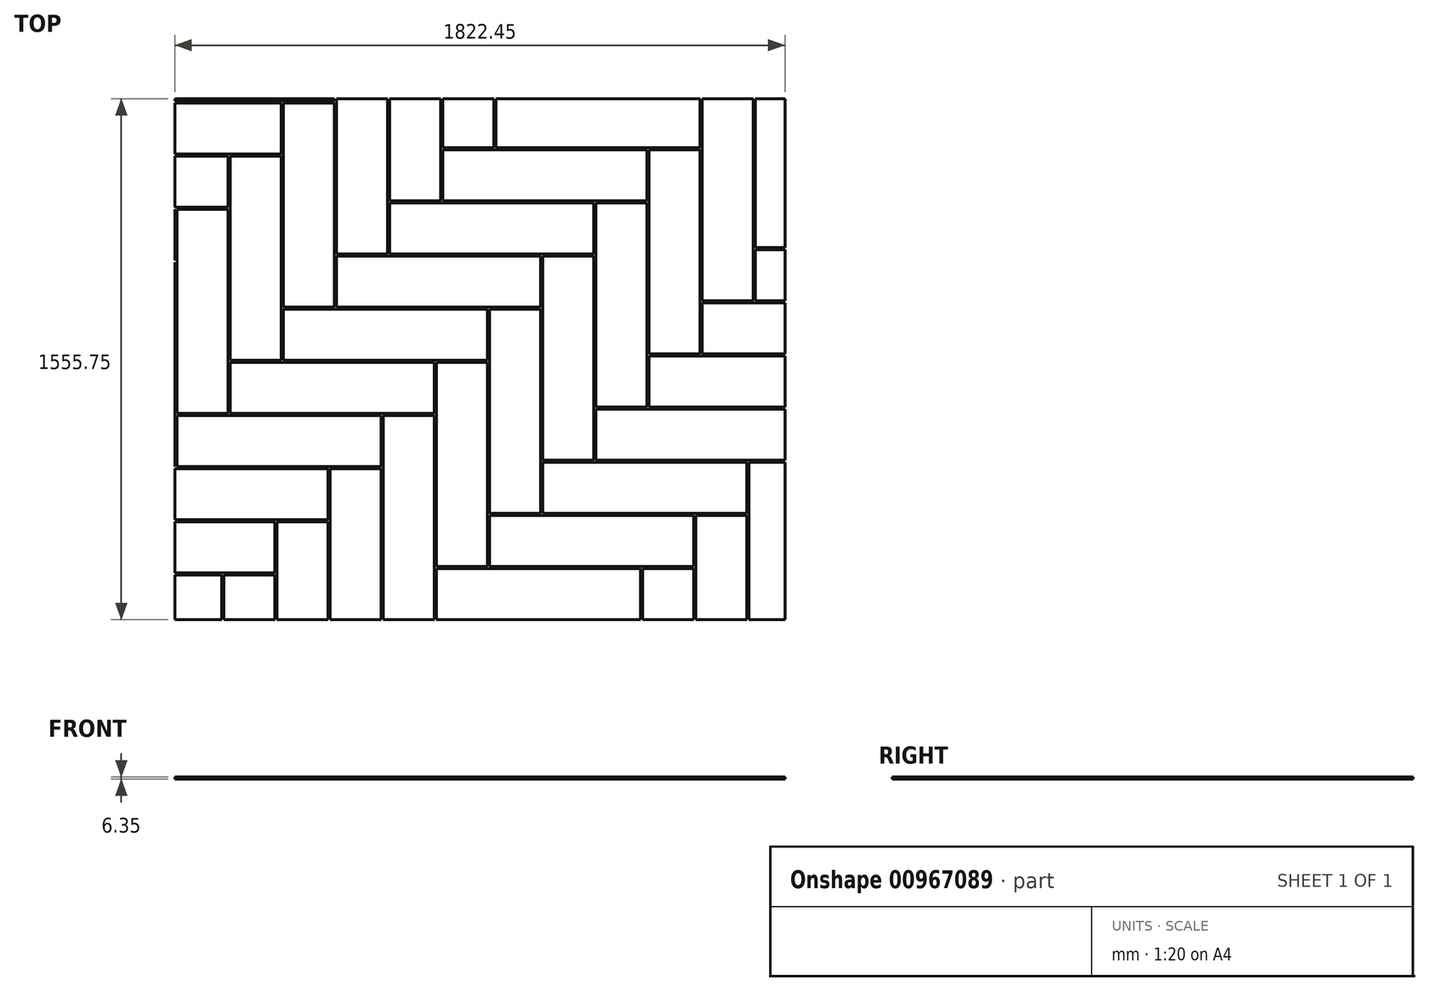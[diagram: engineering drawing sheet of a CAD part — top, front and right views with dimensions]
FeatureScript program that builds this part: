
annotation { "Feature Type Name" : "Feature", "Feature Type Description" : "" }
export const myFeature = defineFeature(function(context is Context, id is Id, definition is map)
    precondition{}
    {
        {
            var Q0;
            Q0=qCreatedBy(makeId("Top.planeOp"),FACE);
            var sketch = newSketch(context, id + "F0", { "sketchPlane" : qUnion([Q0])});
            skLineSegment(sketch, "E0", {"start": v(0, 2298.7) * mm, "end": v(0, 0) * mm});
            skLineSegment(sketch, "E1", {"start": v(0, 0) * mm, "end": v(1822.45, 0) * mm});
            skLineSegment(sketch, "E2", {"start": v(1822.45, 0) * mm, "end": v(1822.45, 1555.75) * mm});
            skLineSegment(sketch, "E3", {"start": v(1822.45, 1555.75) * mm, "end": v(1454.15, 1555.75) * mm});
            skLineSegment(sketch, "E4", {"start": v(1454.15, 1555.75) * mm, "end": v(1454.15, 2298.7) * mm});
            skLineSegment(sketch, "E5", {"start": v(1454.15, 2298.7) * mm, "end": v(0, 2298.7) * mm});
            skSolve(sketch);
        }
        {
            var Q0;
            Q0=qCreatedBy(makeId("Top.planeOp"),FACE);
            var sketch = newSketch(context, id + "F1", { "sketchPlane" : qUnion([Q0])});
            skLineSegment(sketch, "E6", {"start": v(863.6, 0) * mm, "end": v(863.6, -353.23) * mm, "construction": true});
            skLineSegment(sketch, "E7", {"start": v(1631.95, 0) * mm, "end": v(1631.95, -340.06) * mm, "construction": true});
            skLineSegment(sketch, "E8.bottom", {"start": v(781.93, 0) * mm, "end": v(1391.53, 0) * mm});
            skLineSegment(sketch, "E8.top", {"start": v(781.93, 152.4) * mm, "end": v(1391.53, 152.4) * mm});
            skLineSegment(sketch, "E8.left", {"start": v(781.93, 0) * mm, "end": v(781.93, 152.4) * mm});
            skLineSegment(sketch, "E8.right", {"start": v(1391.53, 0) * mm, "end": v(1391.53, 152.4) * mm});
            skLineSegment(sketch, "E9.bottom", {"start": v(781.93, 158.75) * mm, "end": v(934.33, 158.75) * mm});
            skLineSegment(sketch, "E9.top", {"start": v(781.93, 768.35) * mm, "end": v(934.33, 768.35) * mm});
            skLineSegment(sketch, "E9.left", {"start": v(781.93, 158.75) * mm, "end": v(781.93, 768.35) * mm});
            skLineSegment(sketch, "E9.right", {"start": v(934.33, 158.75) * mm, "end": v(934.33, 768.35) * mm});
            skLineSegment(sketch, "E10.bottom", {"start": v(940.68, 158.75) * mm, "end": v(1550.28, 158.75) * mm});
            skLineSegment(sketch, "E10.top", {"start": v(940.68, 311.15) * mm, "end": v(1550.28, 311.15) * mm});
            skLineSegment(sketch, "E10.left", {"start": v(940.68, 158.75) * mm, "end": v(940.68, 311.15) * mm});
            skLineSegment(sketch, "E10.right", {"start": v(1550.28, 158.75) * mm, "end": v(1550.28, 311.15) * mm});
            skLineSegment(sketch, "E11.bottom", {"start": v(940.68, 317.5) * mm, "end": v(1093.08, 317.5) * mm});
            skLineSegment(sketch, "E11.top", {"start": v(940.68, 927.1) * mm, "end": v(1093.08, 927.1) * mm});
            skLineSegment(sketch, "E11.left", {"start": v(940.68, 317.5) * mm, "end": v(940.68, 927.1) * mm});
            skLineSegment(sketch, "E11.right", {"start": v(1093.08, 317.5) * mm, "end": v(1093.08, 927.1) * mm});
            skLineSegment(sketch, "E12.bottom", {"start": v(775.58, 0) * mm, "end": v(623.18, 0) * mm});
            skLineSegment(sketch, "E12.top", {"start": v(775.58, 609.6) * mm, "end": v(623.18, 609.6) * mm});
            skLineSegment(sketch, "E12.left", {"start": v(775.58, 0) * mm, "end": v(775.58, 609.6) * mm});
            skLineSegment(sketch, "E12.right", {"start": v(623.18, 0) * mm, "end": v(623.18, 609.6) * mm});
            skLineSegment(sketch, "E13.bottom", {"start": v(616.83, 609.6) * mm, "end": v(7.23, 609.6) * mm});
            skLineSegment(sketch, "E13.top", {"start": v(616.83, 457.2) * mm, "end": v(7.23, 457.2) * mm});
            skLineSegment(sketch, "E13.left", {"start": v(616.83, 609.6) * mm, "end": v(616.83, 457.2) * mm});
            skLineSegment(sketch, "E13.right", {"start": v(7.23, 609.6) * mm, "end": v(7.23, 457.2) * mm});
            skLineSegment(sketch, "E14.bottom", {"start": v(616.83, 450.85) * mm, "end": v(464.43, 450.85) * mm});
            skLineSegment(sketch, "E14.top", {"start": v(616.83, -158.75) * mm, "end": v(464.43, -158.75) * mm});
            skLineSegment(sketch, "E14.left", {"start": v(616.83, 450.85) * mm, "end": v(616.83, -158.75) * mm});
            skLineSegment(sketch, "E14.right", {"start": v(464.43, 450.85) * mm, "end": v(464.43, -158.75) * mm});
            skLineSegment(sketch, "E15.bottom", {"start": v(458.08, 450.85) * mm, "end": v(-151.52, 450.85) * mm});
            skLineSegment(sketch, "E15.top", {"start": v(458.08, 298.45) * mm, "end": v(-151.52, 298.45) * mm});
            skLineSegment(sketch, "E15.left", {"start": v(458.08, 450.85) * mm, "end": v(458.08, 298.45) * mm});
            skLineSegment(sketch, "E15.right", {"start": v(-151.52, 450.85) * mm, "end": v(-151.52, 298.45) * mm});
            skLineSegment(sketch, "E16.bottom", {"start": v(305.68, 292.1) * mm, "end": v(458.08, 292.1) * mm});
            skLineSegment(sketch, "E16.top", {"start": v(305.68, -317.5) * mm, "end": v(458.08, -317.5) * mm});
            skLineSegment(sketch, "E16.left", {"start": v(305.68, 292.1) * mm, "end": v(305.68, -317.5) * mm});
            skLineSegment(sketch, "E16.right", {"start": v(458.08, 292.1) * mm, "end": v(458.08, -317.5) * mm});
            skLineSegment(sketch, "E17.bottom", {"start": v(299.33, 292.1) * mm, "end": v(-310.27, 292.1) * mm});
            skLineSegment(sketch, "E17.top", {"start": v(299.33, 139.7) * mm, "end": v(-310.27, 139.7) * mm});
            skLineSegment(sketch, "E17.left", {"start": v(299.33, 292.1) * mm, "end": v(299.33, 139.7) * mm});
            skLineSegment(sketch, "E17.right", {"start": v(-310.27, 292.1) * mm, "end": v(-310.27, 139.7) * mm});
            skLineSegment(sketch, "E18.bottom", {"start": v(299.33, 133.35) * mm, "end": v(146.93, 133.35) * mm});
            skLineSegment(sketch, "E18.top", {"start": v(299.33, -476.25) * mm, "end": v(146.93, -476.25) * mm});
            skLineSegment(sketch, "E18.left", {"start": v(299.33, 133.35) * mm, "end": v(299.33, -476.25) * mm});
            skLineSegment(sketch, "E18.right", {"start": v(146.93, 133.35) * mm, "end": v(146.93, -476.25) * mm});
            skLineSegment(sketch, "E19.bottom", {"start": v(140.58, -25.4) * mm, "end": v(-11.82, -25.4) * mm});
            skLineSegment(sketch, "E19.top", {"start": v(140.58, -635) * mm, "end": v(-11.82, -635) * mm});
            skLineSegment(sketch, "E19.left", {"start": v(140.58, -25.4) * mm, "end": v(140.58, -635) * mm});
            skLineSegment(sketch, "E19.right", {"start": v(-11.82, -25.4) * mm, "end": v(-11.82, -635) * mm});
            skLineSegment(sketch, "E20.bottom", {"start": v(140.58, 133.35) * mm, "end": v(-469.02, 133.35) * mm});
            skLineSegment(sketch, "E20.top", {"start": v(140.58, -19.05) * mm, "end": v(-469.02, -19.05) * mm});
            skLineSegment(sketch, "E20.left", {"start": v(140.58, 133.35) * mm, "end": v(140.58, -19.05) * mm});
            skLineSegment(sketch, "E20.right", {"start": v(-469.02, 133.35) * mm, "end": v(-469.02, -19.05) * mm});
            skLineSegment(sketch, "E21.bottom", {"start": v(775.58, 615.95) * mm, "end": v(165.98, 615.95) * mm});
            skLineSegment(sketch, "E21.top", {"start": v(775.58, 768.35) * mm, "end": v(165.98, 768.35) * mm});
            skLineSegment(sketch, "E21.left", {"start": v(775.58, 615.95) * mm, "end": v(775.58, 768.35) * mm});
            skLineSegment(sketch, "E21.right", {"start": v(165.98, 615.95) * mm, "end": v(165.98, 768.35) * mm});
            skLineSegment(sketch, "E22.bottom", {"start": v(934.33, 774.7) * mm, "end": v(324.73, 774.7) * mm});
            skLineSegment(sketch, "E22.top", {"start": v(934.33, 927.1) * mm, "end": v(324.73, 927.1) * mm});
            skLineSegment(sketch, "E22.left", {"start": v(934.33, 774.7) * mm, "end": v(934.33, 927.1) * mm});
            skLineSegment(sketch, "E22.right", {"start": v(324.73, 774.7) * mm, "end": v(324.73, 927.1) * mm});
            skLineSegment(sketch, "E23.bottom", {"start": v(1093.08, 933.45) * mm, "end": v(483.48, 933.45) * mm});
            skLineSegment(sketch, "E23.top", {"start": v(1093.08, 1085.85) * mm, "end": v(483.48, 1085.85) * mm});
            skLineSegment(sketch, "E23.left", {"start": v(1093.08, 933.45) * mm, "end": v(1093.08, 1085.85) * mm});
            skLineSegment(sketch, "E23.right", {"start": v(483.48, 933.45) * mm, "end": v(483.48, 1085.85) * mm});
            skLineSegment(sketch, "E24.bottom", {"start": v(1099.43, 317.5) * mm, "end": v(1709.03, 317.5) * mm});
            skLineSegment(sketch, "E24.top", {"start": v(1099.43, 469.9) * mm, "end": v(1709.03, 469.9) * mm});
            skLineSegment(sketch, "E24.left", {"start": v(1099.43, 317.5) * mm, "end": v(1099.43, 469.9) * mm});
            skLineSegment(sketch, "E24.right", {"start": v(1709.03, 317.5) * mm, "end": v(1709.03, 469.9) * mm});
            skLineSegment(sketch, "E25.bottom", {"start": v(1099.43, 476.25) * mm, "end": v(1251.83, 476.25) * mm});
            skLineSegment(sketch, "E25.top", {"start": v(1099.43, 1085.85) * mm, "end": v(1251.83, 1085.85) * mm});
            skLineSegment(sketch, "E25.left", {"start": v(1099.43, 476.25) * mm, "end": v(1099.43, 1085.85) * mm});
            skLineSegment(sketch, "E25.right", {"start": v(1251.83, 476.25) * mm, "end": v(1251.83, 1085.85) * mm});
            skLineSegment(sketch, "E26.bottom", {"start": v(1258.18, 476.25) * mm, "end": v(1867.78, 476.25) * mm});
            skLineSegment(sketch, "E26.top", {"start": v(1258.18, 628.65) * mm, "end": v(1867.78, 628.65) * mm});
            skLineSegment(sketch, "E26.left", {"start": v(1258.18, 476.25) * mm, "end": v(1258.18, 628.65) * mm});
            skLineSegment(sketch, "E26.right", {"start": v(1867.78, 476.25) * mm, "end": v(1867.78, 628.65) * mm});
            skLineSegment(sketch, "E27.bottom", {"start": v(1258.18, 635) * mm, "end": v(1410.58, 635) * mm});
            skLineSegment(sketch, "E27.top", {"start": v(1258.18, 1244.6) * mm, "end": v(1410.58, 1244.6) * mm});
            skLineSegment(sketch, "E27.left", {"start": v(1258.18, 635) * mm, "end": v(1258.18, 1244.6) * mm});
            skLineSegment(sketch, "E27.right", {"start": v(1410.58, 635) * mm, "end": v(1410.58, 1244.6) * mm});
            skLineSegment(sketch, "E28.bottom", {"start": v(1416.93, 635) * mm, "end": v(2026.53, 635) * mm});
            skLineSegment(sketch, "E28.top", {"start": v(1416.93, 787.4) * mm, "end": v(2026.53, 787.4) * mm});
            skLineSegment(sketch, "E28.left", {"start": v(1416.93, 635) * mm, "end": v(1416.93, 787.4) * mm});
            skLineSegment(sketch, "E28.right", {"start": v(2026.53, 635) * mm, "end": v(2026.53, 787.4) * mm});
            skLineSegment(sketch, "E29.bottom", {"start": v(1251.83, 1244.6) * mm, "end": v(642.23, 1244.6) * mm});
            skLineSegment(sketch, "E29.top", {"start": v(1251.83, 1092.2) * mm, "end": v(642.23, 1092.2) * mm});
            skLineSegment(sketch, "E29.left", {"start": v(1251.83, 1244.6) * mm, "end": v(1251.83, 1092.2) * mm});
            skLineSegment(sketch, "E29.right", {"start": v(642.23, 1244.6) * mm, "end": v(642.23, 1092.2) * mm});
            skLineSegment(sketch, "E30.bottom", {"start": v(1416.93, 793.75) * mm, "end": v(1569.33, 793.75) * mm});
            skLineSegment(sketch, "E30.top", {"start": v(1416.93, 1403.35) * mm, "end": v(1569.33, 1403.35) * mm});
            skLineSegment(sketch, "E30.left", {"start": v(1416.93, 793.75) * mm, "end": v(1416.93, 1403.35) * mm});
            skLineSegment(sketch, "E30.right", {"start": v(1569.33, 793.75) * mm, "end": v(1569.33, 1403.35) * mm});
            skLineSegment(sketch, "E31.bottom", {"start": v(1575.68, 793.75) * mm, "end": v(2185.28, 793.75) * mm});
            skLineSegment(sketch, "E31.top", {"start": v(1575.68, 946.15) * mm, "end": v(2185.28, 946.15) * mm});
            skLineSegment(sketch, "E31.left", {"start": v(1575.68, 793.75) * mm, "end": v(1575.68, 946.15) * mm});
            skLineSegment(sketch, "E31.right", {"start": v(2185.28, 793.75) * mm, "end": v(2185.28, 946.15) * mm});
            skLineSegment(sketch, "E32.bottom", {"start": v(1410.58, 1403.35) * mm, "end": v(800.98, 1403.35) * mm});
            skLineSegment(sketch, "E32.top", {"start": v(1410.58, 1250.95) * mm, "end": v(800.98, 1250.95) * mm});
            skLineSegment(sketch, "E32.left", {"start": v(1410.58, 1403.35) * mm, "end": v(1410.58, 1250.95) * mm});
            skLineSegment(sketch, "E32.right", {"start": v(800.98, 1403.35) * mm, "end": v(800.98, 1250.95) * mm});
            skLineSegment(sketch, "E33.bottom", {"start": v(642.23, 1250.95) * mm, "end": v(794.63, 1250.95) * mm});
            skLineSegment(sketch, "E33.top", {"start": v(642.23, 1860.55) * mm, "end": v(794.63, 1860.55) * mm});
            skLineSegment(sketch, "E33.left", {"start": v(642.23, 1250.95) * mm, "end": v(642.23, 1860.55) * mm});
            skLineSegment(sketch, "E33.right", {"start": v(794.63, 1250.95) * mm, "end": v(794.63, 1860.55) * mm});
            skLineSegment(sketch, "E34.bottom", {"start": v(635.88, 1092.2) * mm, "end": v(483.48, 1092.2) * mm});
            skLineSegment(sketch, "E34.top", {"start": v(635.88, 1701.8) * mm, "end": v(483.48, 1701.8) * mm});
            skLineSegment(sketch, "E34.left", {"start": v(635.88, 1092.2) * mm, "end": v(635.88, 1701.8) * mm});
            skLineSegment(sketch, "E34.right", {"start": v(483.48, 1092.2) * mm, "end": v(483.48, 1701.8) * mm});
            skLineSegment(sketch, "E35.bottom", {"start": v(477.13, 933.45) * mm, "end": v(324.73, 933.45) * mm});
            skLineSegment(sketch, "E35.top", {"start": v(477.13, 1543.05) * mm, "end": v(324.73, 1543.05) * mm});
            skLineSegment(sketch, "E35.left", {"start": v(477.13, 933.45) * mm, "end": v(477.13, 1543.05) * mm});
            skLineSegment(sketch, "E35.right", {"start": v(324.73, 933.45) * mm, "end": v(324.73, 1543.05) * mm});
            skLineSegment(sketch, "E36.bottom", {"start": v(318.38, 774.7) * mm, "end": v(165.98, 774.7) * mm});
            skLineSegment(sketch, "E36.top", {"start": v(318.38, 1384.3) * mm, "end": v(165.98, 1384.3) * mm});
            skLineSegment(sketch, "E36.left", {"start": v(318.38, 774.7) * mm, "end": v(318.38, 1384.3) * mm});
            skLineSegment(sketch, "E36.right", {"start": v(165.98, 774.7) * mm, "end": v(165.98, 1384.3) * mm});
            skLineSegment(sketch, "E37.bottom", {"start": v(159.63, 615.95) * mm, "end": v(7.23, 615.95) * mm});
            skLineSegment(sketch, "E37.top", {"start": v(159.63, 1225.55) * mm, "end": v(7.23, 1225.55) * mm});
            skLineSegment(sketch, "E37.left", {"start": v(159.63, 615.95) * mm, "end": v(159.63, 1225.55) * mm});
            skLineSegment(sketch, "E37.right", {"start": v(7.23, 615.95) * mm, "end": v(7.23, 1225.55) * mm});
            skLineSegment(sketch, "E38.bottom", {"start": v(0.88, 457.2) * mm, "end": v(-151.52, 457.2) * mm});
            skLineSegment(sketch, "E38.top", {"start": v(0.88, 1066.8) * mm, "end": v(-151.52, 1066.8) * mm});
            skLineSegment(sketch, "E38.left", {"start": v(0.88, 457.2) * mm, "end": v(0.88, 1066.8) * mm});
            skLineSegment(sketch, "E38.right", {"start": v(-151.52, 457.2) * mm, "end": v(-151.52, 1066.8) * mm});
            skLineSegment(sketch, "E39.bottom", {"start": v(1397.88, 152.4) * mm, "end": v(1550.28, 152.4) * mm});
            skLineSegment(sketch, "E39.top", {"start": v(1397.88, -457.2) * mm, "end": v(1550.28, -457.2) * mm});
            skLineSegment(sketch, "E39.left", {"start": v(1397.88, 152.4) * mm, "end": v(1397.88, -457.2) * mm});
            skLineSegment(sketch, "E39.right", {"start": v(1550.28, 152.4) * mm, "end": v(1550.28, -457.2) * mm});
            skLineSegment(sketch, "E40.bottom", {"start": v(1556.63, 311.15) * mm, "end": v(1709.03, 311.15) * mm});
            skLineSegment(sketch, "E40.top", {"start": v(1556.63, -298.45) * mm, "end": v(1709.03, -298.45) * mm});
            skLineSegment(sketch, "E40.left", {"start": v(1556.63, 311.15) * mm, "end": v(1556.63, -298.45) * mm});
            skLineSegment(sketch, "E40.right", {"start": v(1709.03, 311.15) * mm, "end": v(1709.03, -298.45) * mm});
            skLineSegment(sketch, "E41.bottom", {"start": v(1715.38, 469.9) * mm, "end": v(1867.78, 469.9) * mm});
            skLineSegment(sketch, "E41.top", {"start": v(1715.38, -139.7) * mm, "end": v(1867.78, -139.7) * mm});
            skLineSegment(sketch, "E41.left", {"start": v(1715.38, 469.9) * mm, "end": v(1715.38, -139.7) * mm});
            skLineSegment(sketch, "E41.right", {"start": v(1867.78, 469.9) * mm, "end": v(1867.78, -139.7) * mm});
            skLineSegment(sketch, "E42.bottom", {"start": v(-157.87, 298.45) * mm, "end": v(-310.27, 298.45) * mm});
            skLineSegment(sketch, "E42.top", {"start": v(-157.87, 908.05) * mm, "end": v(-310.27, 908.05) * mm});
            skLineSegment(sketch, "E42.left", {"start": v(-157.87, 298.45) * mm, "end": v(-157.87, 908.05) * mm});
            skLineSegment(sketch, "E42.right", {"start": v(-310.27, 298.45) * mm, "end": v(-310.27, 908.05) * mm});
            skLineSegment(sketch, "E43.bottom", {"start": v(800.98, 1409.7) * mm, "end": v(953.38, 1409.7) * mm});
            skLineSegment(sketch, "E43.top", {"start": v(800.98, 2019.3) * mm, "end": v(953.38, 2019.3) * mm});
            skLineSegment(sketch, "E43.left", {"start": v(800.98, 1409.7) * mm, "end": v(800.98, 2019.3) * mm});
            skLineSegment(sketch, "E43.right", {"start": v(953.38, 1409.7) * mm, "end": v(953.38, 2019.3) * mm});
            skLineSegment(sketch, "E44.bottom", {"start": v(959.73, 1409.7) * mm, "end": v(1569.33, 1409.7) * mm});
            skLineSegment(sketch, "E44.top", {"start": v(959.73, 1562.1) * mm, "end": v(1569.33, 1562.1) * mm});
            skLineSegment(sketch, "E44.left", {"start": v(959.73, 1409.7) * mm, "end": v(959.73, 1562.1) * mm});
            skLineSegment(sketch, "E44.right", {"start": v(1569.33, 1409.7) * mm, "end": v(1569.33, 1562.1) * mm});
            skLineSegment(sketch, "E45.bottom", {"start": v(-316.62, 139.7) * mm, "end": v(-469.02, 139.7) * mm});
            skLineSegment(sketch, "E45.top", {"start": v(-316.62, 749.3) * mm, "end": v(-469.02, 749.3) * mm});
            skLineSegment(sketch, "E45.left", {"start": v(-316.62, 139.7) * mm, "end": v(-316.62, 749.3) * mm});
            skLineSegment(sketch, "E45.right", {"start": v(-469.02, 139.7) * mm, "end": v(-469.02, 749.3) * mm});
            skLineSegment(sketch, "E46.bottom", {"start": v(-316.62, 908.05) * mm, "end": v(-926.22, 908.05) * mm});
            skLineSegment(sketch, "E46.top", {"start": v(-316.62, 755.65) * mm, "end": v(-926.22, 755.65) * mm});
            skLineSegment(sketch, "E46.left", {"start": v(-316.62, 908.05) * mm, "end": v(-316.62, 755.65) * mm});
            skLineSegment(sketch, "E46.right", {"start": v(-926.22, 908.05) * mm, "end": v(-926.22, 755.65) * mm});
            skLineSegment(sketch, "E47.bottom", {"start": v(-157.87, 1066.8) * mm, "end": v(-767.47, 1066.8) * mm});
            skLineSegment(sketch, "E47.top", {"start": v(-157.87, 914.4) * mm, "end": v(-767.47, 914.4) * mm});
            skLineSegment(sketch, "E47.left", {"start": v(-157.87, 1066.8) * mm, "end": v(-157.87, 914.4) * mm});
            skLineSegment(sketch, "E47.right", {"start": v(-767.47, 1066.8) * mm, "end": v(-767.47, 914.4) * mm});
            skLineSegment(sketch, "E48.bottom", {"start": v(0.88, 1225.55) * mm, "end": v(-608.72, 1225.55) * mm});
            skLineSegment(sketch, "E48.top", {"start": v(0.88, 1073.15) * mm, "end": v(-608.72, 1073.15) * mm});
            skLineSegment(sketch, "E48.left", {"start": v(0.88, 1225.55) * mm, "end": v(0.88, 1073.15) * mm});
            skLineSegment(sketch, "E48.right", {"start": v(-608.72, 1225.55) * mm, "end": v(-608.72, 1073.15) * mm});
            skLineSegment(sketch, "E49.bottom", {"start": v(159.63, 1384.3) * mm, "end": v(-449.97, 1384.3) * mm});
            skLineSegment(sketch, "E49.top", {"start": v(159.63, 1231.9) * mm, "end": v(-449.97, 1231.9) * mm});
            skLineSegment(sketch, "E49.left", {"start": v(159.63, 1384.3) * mm, "end": v(159.63, 1231.9) * mm});
            skLineSegment(sketch, "E49.right", {"start": v(-449.97, 1384.3) * mm, "end": v(-449.97, 1231.9) * mm});
            skLineSegment(sketch, "E50.bottom", {"start": v(318.38, 1543.05) * mm, "end": v(-291.22, 1543.05) * mm});
            skLineSegment(sketch, "E50.top", {"start": v(318.38, 1390.65) * mm, "end": v(-291.22, 1390.65) * mm});
            skLineSegment(sketch, "E50.left", {"start": v(318.38, 1543.05) * mm, "end": v(318.38, 1390.65) * mm});
            skLineSegment(sketch, "E50.right", {"start": v(-291.22, 1543.05) * mm, "end": v(-291.22, 1390.65) * mm});
            skLineSegment(sketch, "E51.bottom", {"start": v(477.13, 1701.8) * mm, "end": v(-132.47, 1701.8) * mm});
            skLineSegment(sketch, "E51.top", {"start": v(477.13, 1549.4) * mm, "end": v(-132.47, 1549.4) * mm});
            skLineSegment(sketch, "E51.left", {"start": v(477.13, 1701.8) * mm, "end": v(477.13, 1549.4) * mm});
            skLineSegment(sketch, "E51.right", {"start": v(-132.47, 1701.8) * mm, "end": v(-132.47, 1549.4) * mm});
            skLineSegment(sketch, "E52.bottom", {"start": v(-138.82, 1549.4) * mm, "end": v(-291.22, 1549.4) * mm});
            skLineSegment(sketch, "E52.top", {"start": v(-138.82, 2159) * mm, "end": v(-291.22, 2159) * mm});
            skLineSegment(sketch, "E52.left", {"start": v(-138.82, 1549.4) * mm, "end": v(-138.82, 2159) * mm});
            skLineSegment(sketch, "E52.right", {"start": v(-291.22, 1549.4) * mm, "end": v(-291.22, 2159) * mm});
            skLineSegment(sketch, "E53.bottom", {"start": v(-297.57, 1390.65) * mm, "end": v(-449.97, 1390.65) * mm});
            skLineSegment(sketch, "E53.top", {"start": v(-297.57, 2000.25) * mm, "end": v(-449.97, 2000.25) * mm});
            skLineSegment(sketch, "E53.left", {"start": v(-297.57, 1390.65) * mm, "end": v(-297.57, 2000.25) * mm});
            skLineSegment(sketch, "E53.right", {"start": v(-449.97, 1390.65) * mm, "end": v(-449.97, 2000.25) * mm});
            skLineSegment(sketch, "E54.bottom", {"start": v(1575.68, 952.5) * mm, "end": v(1728.08, 952.5) * mm});
            skLineSegment(sketch, "E54.top", {"start": v(1575.68, 1562.1) * mm, "end": v(1728.08, 1562.1) * mm});
            skLineSegment(sketch, "E54.left", {"start": v(1575.68, 952.5) * mm, "end": v(1575.68, 1562.1) * mm});
            skLineSegment(sketch, "E54.right", {"start": v(1728.08, 952.5) * mm, "end": v(1728.08, 1562.1) * mm});
            skLineSegment(sketch, "E55.bottom", {"start": v(1734.43, 952.5) * mm, "end": v(2344.03, 952.5) * mm});
            skLineSegment(sketch, "E55.top", {"start": v(1734.43, 1104.9) * mm, "end": v(2344.03, 1104.9) * mm});
            skLineSegment(sketch, "E55.left", {"start": v(1734.43, 952.5) * mm, "end": v(1734.43, 1104.9) * mm});
            skLineSegment(sketch, "E55.right", {"start": v(2344.03, 952.5) * mm, "end": v(2344.03, 1104.9) * mm});
            skLineSegment(sketch, "E56.bottom", {"start": v(1734.43, 1111.25) * mm, "end": v(1886.83, 1111.25) * mm});
            skLineSegment(sketch, "E56.top", {"start": v(1734.43, 1720.85) * mm, "end": v(1886.83, 1720.85) * mm});
            skLineSegment(sketch, "E56.left", {"start": v(1734.43, 1111.25) * mm, "end": v(1734.43, 1720.85) * mm});
            skLineSegment(sketch, "E56.right", {"start": v(1886.83, 1111.25) * mm, "end": v(1886.83, 1720.85) * mm});
            skSolve(sketch);
        }
        {
            var Q0;
            Q0=qSketchRegion(id+"F1",true);
            extrude(context, id + "F2", {"entities" : qUnion([Q0]), "depth" : 6.35 * mm, "offsetDistance" : 25.4 * mm});
        }
        {
            var Q0;
            Q0=qCreatedBy(makeId("Top.planeOp"),FACE);
            var sketch = newSketch(context, id + "F3", { "sketchPlane" : qUnion([Q0])});
            skLineSegment(sketch, "E57.0", {"start": v(0, 1555.75) * mm, "end": v(0, 0) * mm});
            skLineSegment(sketch, "E57.1", {"start": v(0, 0) * mm, "end": v(1822.45, 0) * mm});
            skLineSegment(sketch, "E57.2", {"start": v(1822.45, 0) * mm, "end": v(1822.45, 1555.75) * mm});
            skLineSegment(sketch, "E57.3", {"start": v(1822.45, 1555.75) * mm, "end": v(0, 1555.75) * mm});
            skLineSegment(sketch, "E58.bottom", {"start": v(-1287.42, 2782.55) * mm, "end": v(3002.2, 2782.55) * mm});
            skLineSegment(sketch, "E58.top", {"start": v(-1287.42, -1222.55) * mm, "end": v(3002.2, -1222.55) * mm});
            skLineSegment(sketch, "E58.left", {"start": v(-1287.42, 2782.55) * mm, "end": v(-1287.42, -1222.55) * mm});
            skLineSegment(sketch, "E58.right", {"start": v(3002.2, 2782.55) * mm, "end": v(3002.2, -1222.55) * mm});
            skSolve(sketch);
        }
        {
            var Q0;
            Q0=qSketchRegion(id+"F3",true);
            extrude(context, id + "F4", {"entities" : qUnion([Q0]), "operationType" : NewBodyOperationType.REMOVE, "endBound" : BoundingType.THROUGH_ALL, "depth" : 25.4 * mm, "offsetDistance" : 25.4 * mm});
        }
    });
